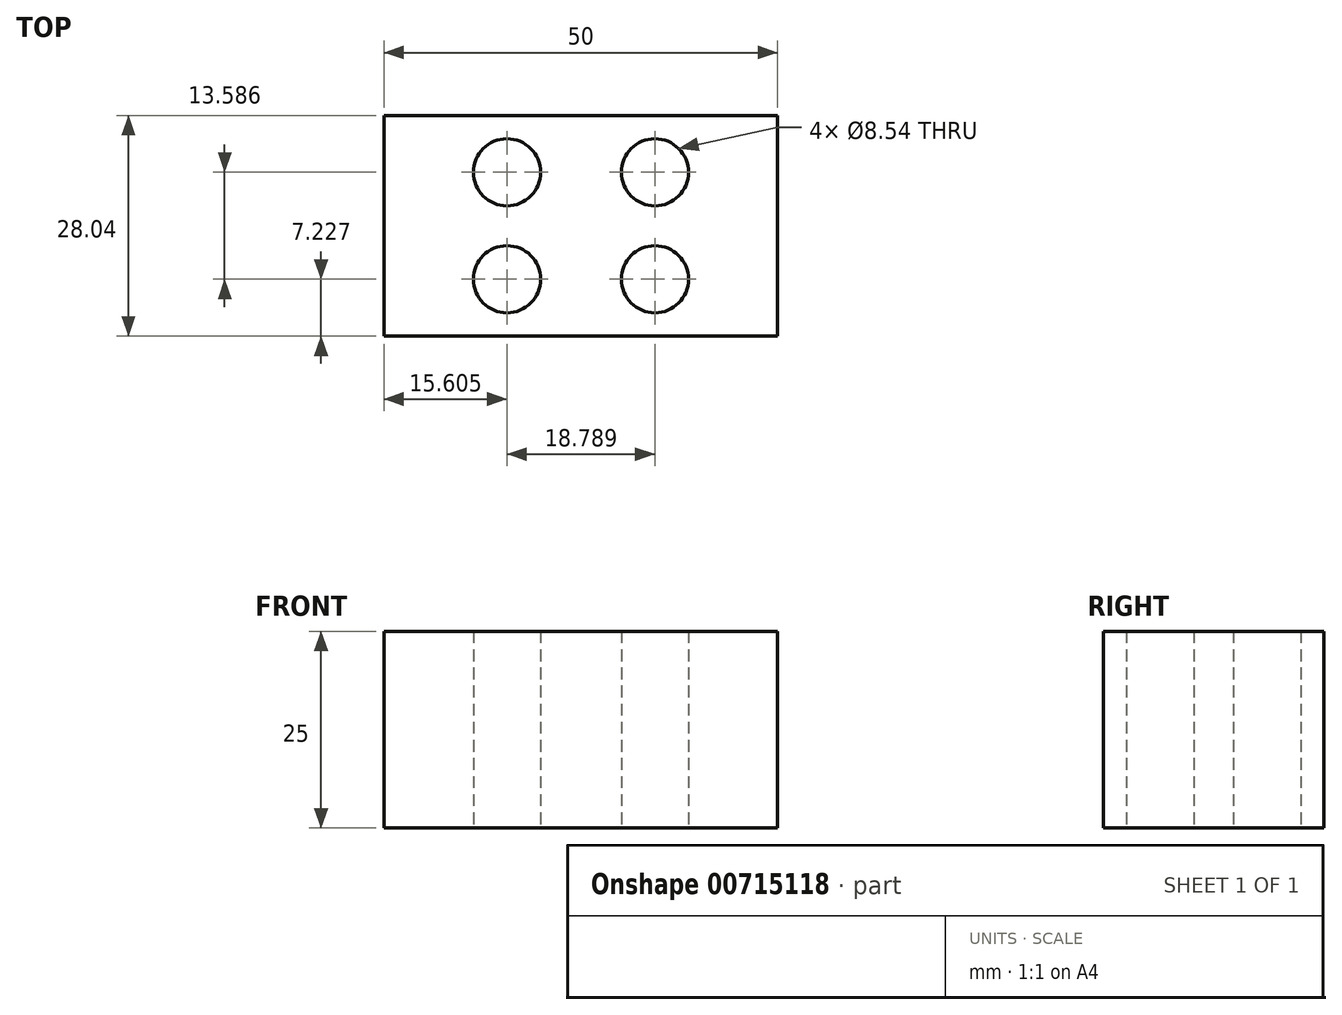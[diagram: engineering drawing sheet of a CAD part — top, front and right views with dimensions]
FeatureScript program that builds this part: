
annotation { "Feature Type Name" : "Feature", "Feature Type Description" : "" }
export const myFeature = defineFeature(function(context is Context, id is Id, definition is map)
    precondition{}
    {
        {
            var Q0;
            Q0=qCreatedBy(makeId("Top.planeOp"),FACE);
            var sketch = newSketch(context, id + "F0", { "sketchPlane" : qUnion([Q0])});
            skLineSegment(sketch, "E0.bottom", {"start": v(25, -14.02) * mm, "end": v(-25, -14.02) * mm});
            skLineSegment(sketch, "E0.top", {"start": v(25, 14.02) * mm, "end": v(-25, 14.02) * mm});
            skLineSegment(sketch, "E0.left", {"start": v(25, -14.02) * mm, "end": v(25, 14.02) * mm});
            skLineSegment(sketch, "E0.right", {"start": v(-25, -14.02) * mm, "end": v(-25, 14.02) * mm});
            skPoint(sketch, "E0.middle", {"position": v(0, 0) * mm});
            skCircle(sketch, "E1", {"center": v(-9.4, 6.8) * mm, "radius": 4.27 * mm});
            skCircle(sketch, "E2", {"center": v(9.4, 6.8) * mm, "radius": 4.27 * mm});
            skCircle(sketch, "E3", {"center": v(-9.4, -6.8) * mm, "radius": 4.27 * mm});
            skCircle(sketch, "E4", {"center": v(9.4, -6.8) * mm, "radius": 4.27 * mm});
            skLineSegment(sketch, "E5", {"start": v(0, -2.17) * mm, "end": v(0, 27.32) * mm, "construction": true});
            skPoint(sketch, "E5.endSnap0", {"position": v(0, 14.02) * mm});
            skLineSegment(sketch, "E6", {"start": v(0, 0) * mm, "end": v(49.86, 0) * mm, "construction": true});
            skSolve(sketch);
        }
        {
            var Q0;
            Q0=makeQuery(id+"F0.imprint","IMPRINT",FACE,{"disambiguationData":[TD([[makeQuery(id+"F0.imprint","IMPRINT",EDGE,{"derivedFrom":sQuery(id+"F0.wireOp",EDGE,"E0.bottom")}),-1.0]])]});
            extrude(context, id + "F1", {"entities" : qUnion([Q0]), "depth" : 25 * mm, "offsetDistance" : 25 * mm});
        }
    });
